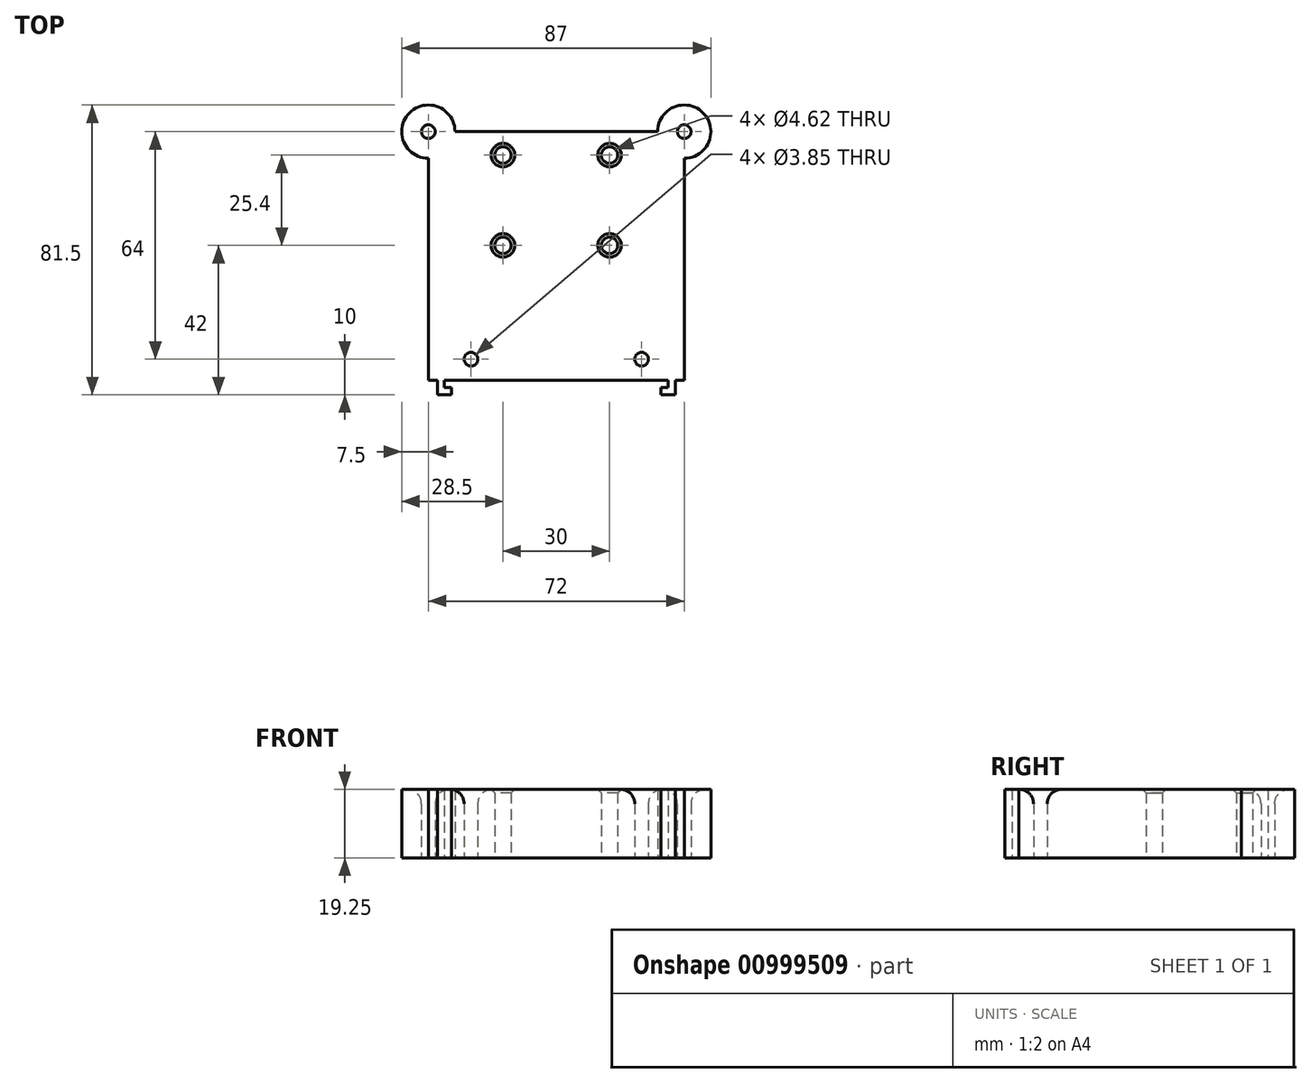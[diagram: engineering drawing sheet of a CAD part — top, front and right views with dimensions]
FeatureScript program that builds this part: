
annotation { "Feature Type Name" : "Feature", "Feature Type Description" : "" }
export const myFeature = defineFeature(function(context is Context, id is Id, definition is map)
    precondition{}
    {
        {
            var Q0;
            Q0=qCreatedBy(makeId("Top.planeOp"),FACE);
            var sketch = newSketch(context, id + "F0", { "sketchPlane" : qUnion([Q0])});
            skLineSegment(sketch, "E0.left", {"start": v(80, -100) * mm, "end": v(80, 100) * mm});
            skLineSegment(sketch, "E0.right", {"start": v(-80, -100) * mm, "end": v(-80, 100) * mm});
            skLineSegment(sketch, "E1.bottom", {"start": v(80, 100) * mm, "end": v(38, 100) * mm});
            skLineSegment(sketch, "E1.top", {"start": v(80, 86) * mm, "end": v(38, 86) * mm});
            skLineSegment(sketch, "E1.left", {"start": v(80, 100) * mm, "end": v(80, 86) * mm});
            skLineSegment(sketch, "E1.right", {"start": v(38, 100) * mm, "end": v(38, 86) * mm});
            skLineSegment(sketch, "E2.bottom", {"start": v(-80, 100) * mm, "end": v(-38, 100) * mm});
            skLineSegment(sketch, "E2.top", {"start": v(-80, 86) * mm, "end": v(-38, 86) * mm});
            skLineSegment(sketch, "E2.left", {"start": v(-80, 100) * mm, "end": v(-80, 86) * mm});
            skLineSegment(sketch, "E2.right", {"start": v(-38, 100) * mm, "end": v(-38, 86) * mm});
            skLineSegment(sketch, "E3.bottom", {"start": v(-27.6, 93.5) * mm, "end": v(27.65, 93.5) * mm});
            skLineSegment(sketch, "E3.top", {"start": v(-27.6, 79.5) * mm, "end": v(27.65, 79.5) * mm});
            skLineSegment(sketch, "E3.left", {"start": v(-27.6, 93.5) * mm, "end": v(-27.6, 79.5) * mm});
            skLineSegment(sketch, "E3.right", {"start": v(27.65, 93.5) * mm, "end": v(27.65, 79.5) * mm});
            skCircle(sketch, "E4", {"center": v(43.25, 93) * mm, "radius": 2.27 * mm});
            skPoint(sketch, "E4.centerSnap0", {"position": v(38, 93) * mm});
            skCircle(sketch, "E5", {"center": v(74.75, 93) * mm, "radius": 2.27 * mm});
            skCircle(sketch, "E6", {"center": v(-43.25, 93) * mm, "radius": 2.27 * mm});
            skPoint(sketch, "E6.centerSnap0", {"position": v(-38, 93) * mm});
            skCircle(sketch, "E7", {"center": v(-74.75, 93) * mm, "radius": 2.27 * mm});
            skPoint(sketch, "E7.centerSnap0", {"position": v(-80, 93) * mm});
            skCircle(sketch, "E8", {"center": v(-21.1, 86.5) * mm, "radius": 2.27 * mm});
            skPoint(sketch, "E8.centerSnap0", {"position": v(-27.6, 86.5) * mm});
            skCircle(sketch, "E9", {"center": v(21.15, 86.5) * mm, "radius": 2.5 * mm});
            skPoint(sketch, "E9.centerSnap0", {"position": v(27.65, 86.5) * mm});
            skLineSegment(sketch, "E10.2", {"start": v(-20, 77.5) * mm, "end": v(20, 77.5) * mm});
            skLineSegment(sketch, "E11.0", {"start": v(82, 102) * mm, "end": v(-82, 102) * mm});
            skLineSegment(sketch, "E11.1", {"start": v(82, -102) * mm, "end": v(82, 102) * mm});
            skLineSegment(sketch, "E11.3", {"start": v(-82, -102.02) * mm, "end": v(-82, 102) * mm});
            skLineSegment(sketch, "E12.0", {"start": v(-82, 84) * mm, "end": v(-36, 84) * mm});
            skLineSegment(sketch, "E12.1", {"start": v(-36, 102) * mm, "end": v(-36, 84) * mm});
            skLineSegment(sketch, "E13.0", {"start": v(82, 84) * mm, "end": v(36, 84) * mm});
            skLineSegment(sketch, "E13.1", {"start": v(36, 102) * mm, "end": v(36, 84) * mm});
            skLineSegment(sketch, "E14", {"start": v(-59, 84) * mm, "end": v(-57.51, -84) * mm});
            skLineSegment(sketch, "E15", {"start": v(59, 84) * mm, "end": v(59, -84) * mm});
            skLineSegment(sketch, "E16", {"start": v(82, 0) * mm, "end": v(80, 0) * mm});
            skLineSegment(sketch, "E17", {"start": v(80, 0) * mm, "end": v(59, 0) * mm});
            skLineSegment(sketch, "E18", {"start": v(59, 0) * mm, "end": v(0, 0) * mm});
            skLineSegment(sketch, "E19", {"start": v(0, 0) * mm, "end": v(-20, 0) * mm});
            skLineSegment(sketch, "E20", {"start": v(-58.26, 0) * mm, "end": v(-80, 0) * mm});
            skLineSegment(sketch, "E21.MirrorCS", {"start": v(-27.6, -93.5) * mm, "end": v(-27.6, -79.5) * mm});
            skCircle(sketch, "E22.MirrorC", {"center": v(-21.1, -86.5) * mm, "radius": 2.27 * mm});
            skCircle(sketch, "E23.MirrorC", {"center": v(74.75, -93) * mm, "radius": 2.27 * mm});
            skCircle(sketch, "E24.MirrorC", {"center": v(-74.75, -93) * mm, "radius": 2.27 * mm});
            skLineSegment(sketch, "E25.MirrorCS", {"start": v(-38, -100) * mm, "end": v(-38, -86) * mm});
            skLineSegment(sketch, "E26.MirrorCS", {"start": v(-36, -102) * mm, "end": v(-36, -84) * mm});
            skCircle(sketch, "E27.MirrorC", {"center": v(43.25, -93) * mm, "radius": 2.27 * mm});
            skCircle(sketch, "E28.MirrorC", {"center": v(21.15, -86.5) * mm, "radius": 2.27 * mm});
            skCircle(sketch, "E29.MirrorC", {"center": v(-43.25, -93) * mm, "radius": 2.27 * mm});
            skLineSegment(sketch, "E30.MirrorCS", {"start": v(27.65, -93.5) * mm, "end": v(27.65, -79.5) * mm});
            skLineSegment(sketch, "E31.MirrorCS", {"start": v(38, -100) * mm, "end": v(38, -86) * mm});
            skPoint(sketch, "E32.MirrorP", {"position": v(-38, -93) * mm});
            skLineSegment(sketch, "E33.MirrorCS", {"start": v(36, -102) * mm, "end": v(36, -84) * mm});
            skLineSegment(sketch, "E34.MirrorCS", {"start": v(80, -100) * mm, "end": v(80, -86) * mm});
            skPoint(sketch, "E35.MirrorP", {"position": v(-27.6, -86.5) * mm});
            skLineSegment(sketch, "E36.MirrorCS", {"start": v(-80, -100) * mm, "end": v(-80, -86) * mm});
            skLineSegment(sketch, "E37.MirrorCS", {"start": v(-82, -84) * mm, "end": v(-36, -84) * mm});
            skLineSegment(sketch, "E38.MirrorCS", {"start": v(-80, -86) * mm, "end": v(-38, -86) * mm});
            skPoint(sketch, "E39.MirrorP", {"position": v(38, -93) * mm});
            skLineSegment(sketch, "E40.MirrorCS", {"start": v(80, -86) * mm, "end": v(38, -86) * mm});
            skLineSegment(sketch, "E41.MirrorCS", {"start": v(-27.6, -79.5) * mm, "end": v(27.65, -79.5) * mm});
            skLineSegment(sketch, "E42.MirrorCS", {"start": v(82, -102) * mm, "end": v(-82, -102) * mm});
            skLineSegment(sketch, "E43.MirrorCS", {"start": v(82, -84) * mm, "end": v(36, -84) * mm});
            skPoint(sketch, "E44.MirrorP", {"position": v(27.65, -86.5) * mm});
            skLineSegment(sketch, "E45.MirrorCS", {"start": v(-27.6, -93.5) * mm, "end": v(27.65, -93.5) * mm});
            skLineSegment(sketch, "E46.MirrorCS", {"start": v(80, -100) * mm, "end": v(38, -100) * mm});
            skPoint(sketch, "E47.MirrorP", {"position": v(-80, -93) * mm});
            skLineSegment(sketch, "E48.MirrorCS", {"start": v(-80, -100) * mm, "end": v(-38, -100) * mm});
            skPoint(sketch, "E49", {"position": v(-80, 0) * mm});
            skPoint(sketch, "E50", {"position": v(-82, 0) * mm});
            skPoint(sketch, "E51", {"position": v(-80, 84) * mm});
            skPoint(sketch, "E52", {"position": v(-82, 84) * mm});
            skPoint(sketch, "E53", {"position": v(80, 84) * mm});
            skPoint(sketch, "E54", {"position": v(82, 84) * mm});
            skPoint(sketch, "E55", {"position": v(80, 0) * mm});
            skPoint(sketch, "E56", {"position": v(82, 0) * mm});
            skLineSegment(sketch, "E57", {"start": v(-82, 84) * mm, "end": v(-80, 84) * mm});
            skLineSegment(sketch, "E58", {"start": v(80, 84) * mm, "end": v(82, 84) * mm});
            skLineSegment(sketch, "E59", {"start": v(36, 102) * mm, "end": v(36, 100) * mm});
            skLineSegment(sketch, "E60", {"start": v(-82, 0) * mm, "end": v(-80, 0) * mm});
            skLineSegment(sketch, "E61", {"start": v(-82, -84) * mm, "end": v(-80, -84) * mm});
            skLineSegment(sketch, "E62", {"start": v(80, -84) * mm, "end": v(82, -84) * mm});
            skLineSegment(sketch, "E63", {"start": v(80, 0) * mm, "end": v(82, 0) * mm});
            skLineSegment(sketch, "E64", {"start": v(-38, 100) * mm, "end": v(-80, 100) * mm});
            skLineSegment(sketch, "E65", {"start": v(-57.51, -84) * mm, "end": v(-58.26, 0) * mm});
            skLineSegment(sketch, "E66", {"start": v(-58.26, 0) * mm, "end": v(-20, 0) * mm});
            skCircle(sketch, "E67.MirrorC", {"center": v(21.15, 86.5) * mm, "radius": 2.27 * mm});
            skLineSegment(sketch, "E68", {"start": v(36, -102) * mm, "end": v(36, -77.5) * mm});
            skLineSegment(sketch, "E69", {"start": v(-36, -102) * mm, "end": v(-36, -77.5) * mm});
            skLineSegment(sketch, "E70", {"start": v(36, -77.5) * mm, "end": v(-36, -77.5) * mm});
            skLineSegment(sketch, "E71", {"start": v(20, -77.5) * mm, "end": v(20, 77.5) * mm});
            skLineSegment(sketch, "E72", {"start": v(-20, 77.5) * mm, "end": v(-20, -77.5) * mm});
            skLineSegment(sketch, "E73", {"start": v(36, 84) * mm, "end": v(36, 77.5) * mm});
            skLineSegment(sketch, "E74", {"start": v(36, 77.5) * mm, "end": v(20, 77.5) * mm});
            skLineSegment(sketch, "E75", {"start": v(-36, 84) * mm, "end": v(-36, 77.5) * mm});
            skLineSegment(sketch, "E76", {"start": v(-20, 77.5) * mm, "end": v(-36, 77.5) * mm});
            skLineSegment(sketch, "E77.bottom", {"start": v(-36, 102) * mm, "end": v(36, 102) * mm});
            skLineSegment(sketch, "E77.top", {"start": v(-36, 172) * mm, "end": v(36, 172) * mm});
            skLineSegment(sketch, "E77.left", {"start": v(-36, 102) * mm, "end": v(-36, 172) * mm});
            skLineSegment(sketch, "E77.right", {"start": v(36, 102) * mm, "end": v(36, 172) * mm});
            skLineSegment(sketch, "E78", {"start": v(0, 102) * mm, "end": v(0, 172) * mm});
            skCircle(sketch, "E79", {"center": v(-15, 140) * mm, "radius": 2.31 * mm});
            skCircle(sketch, "E80", {"center": v(-15, 165.4) * mm, "radius": 2.31 * mm});
            skCircle(sketch, "E81.MirrorC", {"center": v(15, 140) * mm, "radius": 2.31 * mm});
            skCircle(sketch, "E82.MirrorC", {"center": v(15, 165.4) * mm, "radius": 2.31 * mm});
            skLineSegment(sketch, "E83", {"start": v(-33.47, 102) * mm, "end": v(-33.47, 98) * mm});
            skLineSegment(sketch, "E84", {"start": v(-33.47, 98) * mm, "end": v(-29.47, 98) * mm});
            skLineSegment(sketch, "E85", {"start": v(-29.47, 98) * mm, "end": v(-29.47, 100) * mm});
            skLineSegment(sketch, "E86", {"start": v(-29.47, 100) * mm, "end": v(-31.47, 100) * mm});
            skLineSegment(sketch, "E87", {"start": v(-31.47, 100) * mm, "end": v(-31.47, 102) * mm});
            skLineSegment(sketch, "E88.0", {"start": v(-31.27, 100.2) * mm, "end": v(-31.27, 102) * mm});
            skLineSegment(sketch, "E88.1", {"start": v(-33.67, 102) * mm, "end": v(-33.67, 97.8) * mm});
            skLineSegment(sketch, "E88.2", {"start": v(-33.67, 97.8) * mm, "end": v(-29.27, 97.8) * mm});
            skLineSegment(sketch, "E88.3", {"start": v(-29.27, 97.8) * mm, "end": v(-29.27, 100.2) * mm});
            skLineSegment(sketch, "E88.4", {"start": v(-29.27, 100.2) * mm, "end": v(-31.27, 100.2) * mm});
            skLineSegment(sketch, "E89.MirrorCS", {"start": v(31.27, 100.2) * mm, "end": v(31.27, 102) * mm});
            skLineSegment(sketch, "E90.MirrorCS", {"start": v(31.47, 100) * mm, "end": v(31.47, 102) * mm});
            skLineSegment(sketch, "E91.MirrorCS", {"start": v(33.47, 102) * mm, "end": v(33.47, 98) * mm});
            skLineSegment(sketch, "E92.MirrorCS", {"start": v(33.67, 102) * mm, "end": v(33.67, 97.8) * mm});
            skLineSegment(sketch, "E93.MirrorCS", {"start": v(29.27, 97.8) * mm, "end": v(29.27, 100.2) * mm});
            skLineSegment(sketch, "E94.MirrorCS", {"start": v(29.47, 100) * mm, "end": v(31.47, 100) * mm});
            skLineSegment(sketch, "E95.MirrorCS", {"start": v(33.67, 97.8) * mm, "end": v(29.27, 97.8) * mm});
            skLineSegment(sketch, "E96.MirrorCS", {"start": v(29.47, 98) * mm, "end": v(29.47, 100) * mm});
            skLineSegment(sketch, "E97.MirrorCS", {"start": v(29.27, 100.2) * mm, "end": v(31.27, 100.2) * mm});
            skLineSegment(sketch, "E98.MirrorCS", {"start": v(33.47, 98) * mm, "end": v(29.47, 98) * mm});
            skLineSegment(sketch, "E99", {"start": v(-39.13, 0) * mm, "end": v(-39.13, -2.14) * mm});
            skLineSegment(sketch, "E100", {"start": v(-39.13, -2.14) * mm, "end": v(-37.13, -2.14) * mm});
            skLineSegment(sketch, "E101", {"start": v(-37.13, -2.14) * mm, "end": v(-37.13, -4.14) * mm});
            skLineSegment(sketch, "E102", {"start": v(-37.13, -4.14) * mm, "end": v(-43.13, -4.14) * mm});
            skLineSegment(sketch, "E103", {"start": v(-43.13, -4.14) * mm, "end": v(-43.13, -2.14) * mm});
            skLineSegment(sketch, "E104", {"start": v(-43.13, -2.14) * mm, "end": v(-41.13, -2.15) * mm});
            skLineSegment(sketch, "E105", {"start": v(-41.13, -2.15) * mm, "end": v(-41.13, 0) * mm});
            skLineSegment(sketch, "E106.0", {"start": v(-41.38, -1.9) * mm, "end": v(-41.38, 0) * mm});
            skLineSegment(sketch, "E106.1", {"start": v(-43.38, -1.89) * mm, "end": v(-41.38, -1.9) * mm});
            skLineSegment(sketch, "E106.2", {"start": v(-43.38, -4.39) * mm, "end": v(-43.38, -1.89) * mm});
            skLineSegment(sketch, "E106.3", {"start": v(-38.88, 0) * mm, "end": v(-38.88, -1.89) * mm});
            skLineSegment(sketch, "E106.4", {"start": v(-38.88, -1.89) * mm, "end": v(-36.88, -1.89) * mm});
            skLineSegment(sketch, "E106.5", {"start": v(-36.88, -1.89) * mm, "end": v(-36.88, -4.39) * mm});
            skLineSegment(sketch, "E106.6", {"start": v(-36.88, -4.39) * mm, "end": v(-43.38, -4.39) * mm});
            skLineSegment(sketch, "E107.MirrorCS", {"start": v(43.13, -2.14) * mm, "end": v(41.13, -2.15) * mm});
            skLineSegment(sketch, "E108.MirrorCS", {"start": v(39.13, -2.14) * mm, "end": v(37.13, -2.14) * mm});
            skLineSegment(sketch, "E109.MirrorCS", {"start": v(36.88, -4.39) * mm, "end": v(43.38, -4.39) * mm});
            skLineSegment(sketch, "E110.MirrorCS", {"start": v(43.38, -1.89) * mm, "end": v(41.38, -1.9) * mm});
            skLineSegment(sketch, "E111.MirrorCS", {"start": v(37.13, -4.14) * mm, "end": v(43.13, -4.14) * mm});
            skLineSegment(sketch, "E112.MirrorCS", {"start": v(36.88, -1.89) * mm, "end": v(36.88, -4.39) * mm});
            skLineSegment(sketch, "E113.MirrorCS", {"start": v(43.38, -4.39) * mm, "end": v(43.38, -1.89) * mm});
            skLineSegment(sketch, "E114.MirrorCS", {"start": v(38.88, -1.89) * mm, "end": v(36.88, -1.89) * mm});
            skLineSegment(sketch, "E115.MirrorCS", {"start": v(43.13, -4.14) * mm, "end": v(43.13, -2.14) * mm});
            skLineSegment(sketch, "E116.MirrorCS", {"start": v(37.13, -2.14) * mm, "end": v(37.13, -4.14) * mm});
            skLineSegment(sketch, "E117.MirrorCS", {"start": v(41.38, -1.9) * mm, "end": v(41.38, 0) * mm});
            skLineSegment(sketch, "E118.MirrorCS", {"start": v(41.13, -2.15) * mm, "end": v(41.13, 0) * mm});
            skLineSegment(sketch, "E119.MirrorCS", {"start": v(39.13, 0) * mm, "end": v(39.13, -2.14) * mm});
            skLineSegment(sketch, "E120.MirrorCS", {"start": v(38.88, 0) * mm, "end": v(38.88, -1.89) * mm});
            skLineSegment(sketch, "E121.MirrorCS", {"start": v(-29.27, -100.2) * mm, "end": v(-31.27, -100.2) * mm});
            skLineSegment(sketch, "E122.MirrorCS", {"start": v(-29.27, -97.8) * mm, "end": v(-29.27, -100.2) * mm});
            skLineSegment(sketch, "E123.MirrorCS", {"start": v(-33.47, -98) * mm, "end": v(-29.47, -98) * mm});
            skLineSegment(sketch, "E124.MirrorCS", {"start": v(-29.47, -100) * mm, "end": v(-31.47, -100) * mm});
            skLineSegment(sketch, "E125.MirrorCS", {"start": v(-29.47, -98) * mm, "end": v(-29.47, -100) * mm});
            skLineSegment(sketch, "E126.MirrorCS", {"start": v(-33.67, -97.8) * mm, "end": v(-29.27, -97.8) * mm});
            skLineSegment(sketch, "E127.MirrorCS", {"start": v(-33.67, -102) * mm, "end": v(-33.67, -97.8) * mm});
            skLineSegment(sketch, "E128.MirrorCS", {"start": v(-33.47, -102) * mm, "end": v(-33.47, -98) * mm});
            skLineSegment(sketch, "E129.MirrorCS", {"start": v(-31.47, -100) * mm, "end": v(-31.47, -102) * mm});
            skLineSegment(sketch, "E130.MirrorCS", {"start": v(-31.27, -100.2) * mm, "end": v(-31.27, -102) * mm});
            skLineSegment(sketch, "E131.MirrorCS", {"start": v(29.27, -97.8) * mm, "end": v(29.27, -100.2) * mm});
            skLineSegment(sketch, "E132.MirrorCS", {"start": v(29.27, -100.2) * mm, "end": v(31.27, -100.2) * mm});
            skLineSegment(sketch, "E133.MirrorCS", {"start": v(29.47, -98) * mm, "end": v(29.47, -100) * mm});
            skLineSegment(sketch, "E134.MirrorCS", {"start": v(29.47, -100) * mm, "end": v(31.47, -100) * mm});
            skLineSegment(sketch, "E135.MirrorCS", {"start": v(33.67, -97.8) * mm, "end": v(29.27, -97.8) * mm});
            skLineSegment(sketch, "E136.MirrorCS", {"start": v(33.47, -98) * mm, "end": v(29.47, -98) * mm});
            skLineSegment(sketch, "E137.MirrorCS", {"start": v(33.47, -102) * mm, "end": v(33.47, -98) * mm});
            skLineSegment(sketch, "E138.MirrorCS", {"start": v(33.67, -102) * mm, "end": v(33.67, -97.8) * mm});
            skLineSegment(sketch, "E139.MirrorCS", {"start": v(31.47, -100) * mm, "end": v(31.47, -102) * mm});
            skLineSegment(sketch, "E140.MirrorCS", {"start": v(31.27, -100.2) * mm, "end": v(31.27, -102) * mm});
            skCircle(sketch, "E141", {"center": v(36, 172) * mm, "radius": 7.5 * mm});
            skCircle(sketch, "E142.MirrorC", {"center": v(-36, 172) * mm, "radius": 7.5 * mm});
            skCircle(sketch, "E143", {"center": v(82, 102) * mm, "radius": 7.5 * mm});
            skCircle(sketch, "E144", {"center": v(82, -102) * mm, "radius": 7.5 * mm});
            skCircle(sketch, "E145", {"center": v(82, -102) * mm, "radius": 1.88 * mm});
            skCircle(sketch, "E146", {"center": v(82, 102) * mm, "radius": 1.88 * mm});
            skCircle(sketch, "E147", {"center": v(36, 172) * mm, "radius": 1.93 * mm});
            skCircle(sketch, "E148.MirrorC", {"center": v(-36, 172) * mm, "radius": 1.93 * mm});
            skCircle(sketch, "E149.MirrorC", {"center": v(-82, 102) * mm, "radius": 1.88 * mm});
            skCircle(sketch, "E150.MirrorC", {"center": v(-82, 102) * mm, "radius": 7.5 * mm});
            skCircle(sketch, "E151.MirrorC", {"center": v(-82, -102) * mm, "radius": 1.88 * mm});
            skCircle(sketch, "E152.MirrorC", {"center": v(-82, -102) * mm, "radius": 7.5 * mm});
            skCircle(sketch, "E153", {"center": v(24, 108) * mm, "radius": 1.93 * mm});
            skCircle(sketch, "E154.MirrorC", {"center": v(-24, 108) * mm, "radius": 1.93 * mm});
            skCircle(sketch, "E155", {"center": v(20, 97.8) * mm, "radius": 1.88 * mm});
            skLineSegment(sketch, "E156", {"start": v(0, 102) * mm, "end": v(0, 93.5) * mm});
            skPoint(sketch, "E157", {"position": v(0, 97.75) * mm});
            skCircle(sketch, "E158.MirrorC", {"center": v(-20, 97.8) * mm, "radius": 1.88 * mm});
            skCircle(sketch, "E159.MirrorC", {"center": v(-20, -97.8) * mm, "radius": 1.88 * mm});
            skCircle(sketch, "E160.MirrorC", {"center": v(20, -97.8) * mm, "radius": 1.88 * mm});
            skCircle(sketch, "E161", {"center": v(0, -8) * mm, "radius": 1.88 * mm});
            skCircle(sketch, "E162", {"center": v(69.5, -8) * mm, "radius": 1.88 * mm});
            skPoint(sketch, "E162.centerSnap0", {"position": v(69.5, 0) * mm});
            skCircle(sketch, "E163.MirrorC", {"center": v(-69.5, -8) * mm, "radius": 1.88 * mm});
            skCircle(sketch, "E164.MirrorC", {"center": v(-69.5, 8) * mm, "radius": 1.88 * mm});
            skCircle(sketch, "E165.MirrorC", {"center": v(0, 8) * mm, "radius": 1.88 * mm});
            skCircle(sketch, "E166.MirrorC", {"center": v(69.5, 8) * mm, "radius": 1.88 * mm});
            skCircle(sketch, "E167", {"center": v(28, 71.5) * mm, "radius": 1.88 * mm});
            skCircle(sketch, "E168.MirrorC", {"center": v(-28, 71.5) * mm, "radius": 1.88 * mm});
            skCircle(sketch, "E169.MirrorC", {"center": v(28, -71.5) * mm, "radius": 1.88 * mm});
            skCircle(sketch, "E170.MirrorC", {"center": v(-28, -71.5) * mm, "radius": 1.88 * mm});
            skLineSegment(sketch, "E171", {"start": v(41.38, 0) * mm, "end": v(41.13, 0) * mm});
            skLineSegment(sketch, "E172", {"start": v(41.13, 0) * mm, "end": v(39.13, 0) * mm});
            skLineSegment(sketch, "E173", {"start": v(39.13, 0) * mm, "end": v(38.88, 0) * mm});
            skLineSegment(sketch, "E174", {"start": v(41.38, 0) * mm, "end": v(38.88, 0) * mm});
            skLineSegment(sketch, "E175", {"start": v(-38.88, 0) * mm, "end": v(-41.38, 0) * mm});
            skLineSegment(sketch, "E176.MirrorCS", {"start": v(-38.88, 0) * mm, "end": v(-38.88, 1.87) * mm});
            skLineSegment(sketch, "E177.MirrorCS", {"start": v(-43.38, 1.87) * mm, "end": v(-41.38, 1.88) * mm});
            skLineSegment(sketch, "E178.MirrorCS", {"start": v(-43.13, 2.13) * mm, "end": v(-41.13, 2.13) * mm});
            skLineSegment(sketch, "E179.MirrorCS", {"start": v(-43.38, 4.37) * mm, "end": v(-43.38, 1.87) * mm});
            skLineSegment(sketch, "E180.MirrorCS", {"start": v(-41.38, 1.88) * mm, "end": v(-41.38, -0.01) * mm});
            skLineSegment(sketch, "E181.MirrorCS", {"start": v(-37.13, 2.12) * mm, "end": v(-37.13, 4.12) * mm});
            skLineSegment(sketch, "E182.MirrorCS", {"start": v(-43.13, 4.12) * mm, "end": v(-43.13, 2.13) * mm});
            skLineSegment(sketch, "E183.MirrorCS", {"start": v(-39.13, 2.12) * mm, "end": v(-37.13, 2.12) * mm});
            skLineSegment(sketch, "E184.MirrorCS", {"start": v(-36.88, 4.37) * mm, "end": v(-43.38, 4.37) * mm});
            skLineSegment(sketch, "E185.MirrorCS", {"start": v(-37.13, 4.12) * mm, "end": v(-43.13, 4.12) * mm});
            skLineSegment(sketch, "E186.MirrorCS", {"start": v(-36.88, 1.87) * mm, "end": v(-36.88, 4.37) * mm});
            skLineSegment(sketch, "E187.MirrorCS", {"start": v(-38.88, 1.87) * mm, "end": v(-36.88, 1.87) * mm});
            skLineSegment(sketch, "E188.MirrorCS", {"start": v(-39.13, 0) * mm, "end": v(-39.13, 2.12) * mm});
            skLineSegment(sketch, "E189.MirrorCS", {"start": v(-41.13, 2.13) * mm, "end": v(-41.13, -0.01) * mm});
            skLineSegment(sketch, "E190.MirrorCS", {"start": v(-38.88, 0) * mm, "end": v(-41.38, -0.01) * mm});
            skLineSegment(sketch, "E191.MirrorCS", {"start": v(43.13, 2.14) * mm, "end": v(41.13, 2.14) * mm});
            skLineSegment(sketch, "E192.MirrorCS", {"start": v(39.13, 2.14) * mm, "end": v(37.13, 2.14) * mm});
            skLineSegment(sketch, "E193.MirrorCS", {"start": v(41.38, 1.9) * mm, "end": v(41.38, 0) * mm});
            skLineSegment(sketch, "E194.MirrorCS", {"start": v(43.13, 4.14) * mm, "end": v(43.13, 2.14) * mm});
            skLineSegment(sketch, "E195.MirrorCS", {"start": v(37.13, 2.14) * mm, "end": v(37.13, 4.14) * mm});
            skLineSegment(sketch, "E196.MirrorCS", {"start": v(41.13, 2.14) * mm, "end": v(41.13, 0) * mm});
            skLineSegment(sketch, "E197.MirrorCS", {"start": v(43.38, 1.89) * mm, "end": v(41.38, 1.9) * mm});
            skLineSegment(sketch, "E198.MirrorCS", {"start": v(36.88, 1.89) * mm, "end": v(36.88, 4.39) * mm});
            skLineSegment(sketch, "E199.MirrorCS", {"start": v(37.13, 4.14) * mm, "end": v(43.13, 4.14) * mm});
            skLineSegment(sketch, "E200.MirrorCS", {"start": v(38.88, 1.89) * mm, "end": v(36.88, 1.89) * mm});
            skLineSegment(sketch, "E201.MirrorCS", {"start": v(39.13, 0) * mm, "end": v(39.13, 2.14) * mm});
            skLineSegment(sketch, "E202.MirrorCS", {"start": v(36.88, 4.39) * mm, "end": v(43.38, 4.39) * mm});
            skLineSegment(sketch, "E203.MirrorCS", {"start": v(38.88, 0) * mm, "end": v(38.88, 1.89) * mm});
            skLineSegment(sketch, "E204.MirrorCS", {"start": v(43.38, 4.39) * mm, "end": v(43.38, 1.89) * mm});
            skLineSegment(sketch, "E205", {"start": v(38.88, 0) * mm, "end": v(38.88, 0) * mm});
            skLineSegment(sketch, "E206", {"start": v(33.67, 102) * mm, "end": v(31.27, 102) * mm});
            skLineSegment(sketch, "E207", {"start": v(-31.27, 102) * mm, "end": v(-33.67, 102) * mm});
            skSolve(sketch);
        }
        {
            var Q0;
            {var subQ4=sQuery(id+"F0.wireOp",EDGE,"E78");Q0=makeQuery(id+"F0.imprint","IMPRINT",FACE,{"disambiguationData":[TD([[makeQuery(id+"F0.imprint","IMPRINT",EDGE,{"derivedFrom":subQ4}),-1.0]])]});}
            var Q1;
            {var subQ11=sQuery(id+"F0.wireOp",EDGE,"E78");Q1=makeQuery(id+"F0.imprint","IMPRINT",FACE,{"disambiguationData":[TD([[makeQuery(id+"F0.imprint","IMPRINT",EDGE,{"derivedFrom":subQ11}),1.0]])]});}
            var Q2;
            {var subQ0=sQuery(id+"F0.wireOp",EDGE,"E83");Q2=makeQuery(id+"F0.imprint","IMPRINT",FACE,{"disambiguationData":[TD([[makeQuery(id+"F0.imprint","IMPRINT",EDGE,{"derivedFrom":subQ0}),1.0]])]});}
            var Q3;
            {var subQ1=sQuery(id+"F0.wireOp",EDGE,"E90.MirrorCS");Q3=makeQuery(id+"F0.imprint","IMPRINT",FACE,{"disambiguationData":[TD([[makeQuery(id+"F0.imprint","IMPRINT",EDGE,{"derivedFrom":subQ1}),-1.0]])]});}
            var Q4;
            {var subQ0=sQuery(id+"F0.wireOp",EDGE,"E142.MirrorC");var subQ1=sQuery(id+"F0.wireOp",EDGE,"E77.top");var subQ2=makeQuery(id+"F0.imprint","INTERSECT",VERTEX,{"derivedFrom":[subQ1,subQ0]});Q4=makeQuery(id+"F0.imprint","IMPRINT",FACE,{"disambiguationData":[TD([[makeQuery(id+"F0.imprint","IMPRINT",EDGE,{"disambiguationData":[TD([[subQ2,1.0]])],"derivedFrom":subQ1}),-1.0]])]});}
            var Q5;
            {var subQ0=sQuery(id+"F0.wireOp",EDGE,"E142.MirrorC");var subQ1=sQuery(id+"F0.wireOp",EDGE,"E77.top");var subQ2=makeQuery(id+"F0.imprint","INTERSECT",VERTEX,{"derivedFrom":[subQ1,subQ0]});Q5=makeQuery(id+"F0.imprint","IMPRINT",FACE,{"disambiguationData":[TD([[makeQuery(id+"F0.imprint","IMPRINT",EDGE,{"disambiguationData":[TD([[subQ2,1.0]])],"derivedFrom":subQ1}),1.0]])]});}
            var Q6;
            {var subQ0=sQuery(id+"F0.wireOp",EDGE,"E141");var subQ1=sQuery(id+"F0.wireOp",EDGE,"E77.top");var subQ2=makeQuery(id+"F0.imprint","INTERSECT",VERTEX,{"derivedFrom":[subQ1,subQ0]});Q6=makeQuery(id+"F0.imprint","IMPRINT",FACE,{"disambiguationData":[TD([[makeQuery(id+"F0.imprint","IMPRINT",EDGE,{"disambiguationData":[TD([[subQ2,-1.0]])],"derivedFrom":subQ1}),1.0]])]});}
            var Q7;
            {var subQ0=sQuery(id+"F0.wireOp",EDGE,"E141");var subQ1=sQuery(id+"F0.wireOp",EDGE,"E77.top");var subQ2=makeQuery(id+"F0.imprint","INTERSECT",VERTEX,{"derivedFrom":[subQ1,subQ0]});Q7=makeQuery(id+"F0.imprint","IMPRINT",FACE,{"disambiguationData":[TD([[makeQuery(id+"F0.imprint","IMPRINT",EDGE,{"disambiguationData":[TD([[subQ2,-1.0]])],"derivedFrom":subQ1}),-1.0]])]});}
            extrude(context, id + "F1", {"entities" : qUnion([Q0, Q1, Q2, Q3, Q4, Q5, Q6, Q7]), "depth" : 19.25 * mm, "offsetDistance" : 25 * mm});
        }
        {
            var Q0;
            Q0=makeQuery(id+"F1.opExtrude","CAP_EDGE",EDGE,{"disambiguationData":[OSD([sQuery(id+"F0.wireOp",EDGE,"E148.MirrorC")])],"isStart":false});
            var Q1;
            Q1=makeQuery(id+"F1.opExtrude","CAP_EDGE",EDGE,{"disambiguationData":[OSD([sQuery(id+"F0.wireOp",EDGE,"E154.MirrorC")])],"isStart":false});
            var Q2;
            Q2=makeQuery(id+"F1.opExtrude","CAP_EDGE",EDGE,{"disambiguationData":[OSD([sQuery(id+"F0.wireOp",EDGE,"E153")])],"isStart":false});
            var Q3;
            Q3=makeQuery(id+"F1.opExtrude","CAP_EDGE",EDGE,{"disambiguationData":[OSD([sQuery(id+"F0.wireOp",EDGE,"E147")])],"isStart":false});
            fillet(context, id + "F2", {"entities" : qUnion([Q0, Q1, Q2, Q3]), "radius" : 4 * mm, "tangentPropagation" : true, "allowEdgeOverflow" : false});
        }
        {
            var Q0;
            Q0=makeQuery(id+"F1.opExtrude","CAP_EDGE",EDGE,{"disambiguationData":[OSD([sQuery(id+"F0.wireOp",EDGE,"E80")])],"isStart":false});
            var Q1;
            Q1=makeQuery(id+"F1.opExtrude","CAP_EDGE",EDGE,{"disambiguationData":[OSD([sQuery(id+"F0.wireOp",EDGE,"E79")])],"isStart":false});
            var Q2;
            Q2=makeQuery(id+"F1.opExtrude","CAP_EDGE",EDGE,{"disambiguationData":[OSD([sQuery(id+"F0.wireOp",EDGE,"E81.MirrorC")])],"isStart":false});
            var Q3;
            Q3=makeQuery(id+"F1.opExtrude","CAP_EDGE",EDGE,{"disambiguationData":[OSD([sQuery(id+"F0.wireOp",EDGE,"E82.MirrorC")])],"isStart":false});
            chamfer(context, id + "F3", {"entities" : qUnion([Q0, Q1, Q2, Q3]), "width" : 1 * mm, "tangentPropagation" : true});
        }
    });
